# Revit family: Building-SurfaceMountingEnclosures-GEWISS-42TV-WORKBENCH_TOWER-IP55
name_source: partatom
category: Attrezzatura elettrica
revit_build: Autodesk Revit 2016 (Build: 20161004_0715(x64)
units: mm (PartAtom-declared; Revit-internal decimal feet)

## family parameters
Basato su piano di lavoro = No
Condiviso = No
Configurazione quadro = Due colonne, circuiti in orizzontale
Numero OmniClass = 23.60.00.00
Punto di calcolo locali = Sì
Quota connettore circolare = Usa diametro
Sempre verticale = Sì
Taglio con vuoti quando caricato = No
Tipo di parte = Pannello comandi
Titolo OmniClass = General Purpose: Services

## types (1)
- GW68441 - FLOOR M.TOWER 295X200X180 IP55
    Altezza torretta = 295 mm  [stored 0.967848 ft]
    Basamento = 180 mm  [stored 0.590551 ft]
    Catalogue = BUILDING
    Catalogue Range = 42 TV
    Characteristics = Halogen free
    Colour = Grey RAL 7035
    Descrizione = FLOOR M.TOWER 295X200X180 IP55
    Diametro entrata corrugati = 50 mm  [stored 0.164042 ft]
    EAN code = 8011564033528
    Electrocod = 2202
    Glow Wire Test = 650°C
    Houseable IB socket-outlets = 16/32 A
    IDF = 07b33a41-a608-41c2-9237-38cd567f3d24
    IDT = 63329205-fc50-4150-ad5f-9bf692c0f363
    IP degree = IP55
    Immagine tipo = GW68441.jpg
    Installable Q-DIN boards = Q-DIN 5
    Insulation class = II
    Lunghezza torretta = 200 mm  [stored 0.656168 ft]
    Modello = GW68441
    Numero poli = 1
    Operating temperature: = -25 +40 °C
    Outer dim. LxHxD (mm) = 200x295x180
    Potenza in watt = 0 V
    Produttore = GEWISS S.p.A.
    SEO = Tower
    Shock resistance = IK08
    Spessore torretta = 54 mm  [stored 0.177165 ft]
    Technical sheet = https://www.gewiss.com
    Thermo-pressure with ball = 70
    Torretta = <Per categoria>
    URL = https://www.gewiss.com
    Version file RFA = 18.0
    Working temperature = -25 +40 °C

note: source unit labels omitted for Thermo-pressure with ball — the stored unit's dimension contradicts the parameter name (converter mislabeling)

note: [stored X ft] marks values corroborated as IEEE doubles in the binary element streams (Revit-internal decimal feet)

## geometry (parser evidence)
native form markers: Sweep x1
no freeform markers — native parametric forms only
